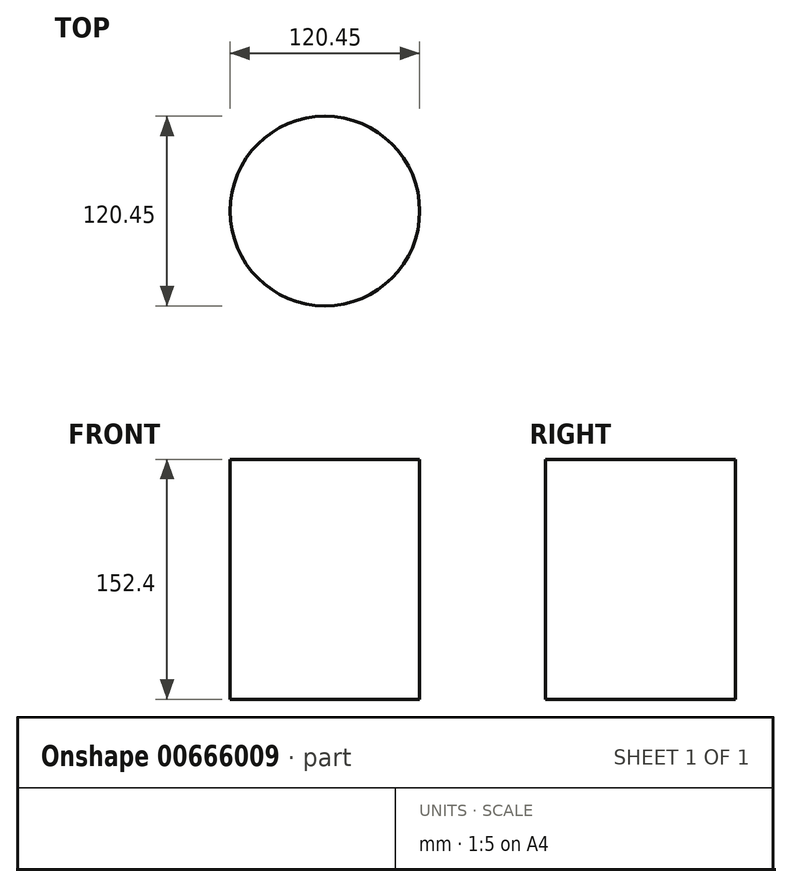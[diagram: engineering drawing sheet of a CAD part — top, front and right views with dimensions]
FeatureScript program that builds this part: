
annotation { "Feature Type Name" : "Feature", "Feature Type Description" : "" }
export const myFeature = defineFeature(function(context is Context, id is Id, definition is map)
    precondition{}
    {
        {
            var Q0;
            Q0=qCreatedBy(makeId("Top.planeOp"),FACE);
            var sketch = newSketch(context, id + "F0", { "sketchPlane" : qUnion([Q0])});
            skCircle(sketch, "E0", {"center": v(-58.57, 2.67) * mm, "radius": 60.22 * mm});
            skSolve(sketch);
        }
        {
            var Q0;
            Q0=makeQuery(id+"F0.imprint","IMPRINT",FACE,{"disambiguationData":[TD([[makeQuery(id+"F0.imprint","IMPRINT",EDGE,{"derivedFrom":sQuery(id+"F0.wireOp",EDGE,"E0")}),1.0]])]});
            extrude(context, id + "F1", {"entities" : qUnion([Q0]), "depth" : 152.4 * mm, "offsetDistance" : 25.4 * mm});
        }
    });
